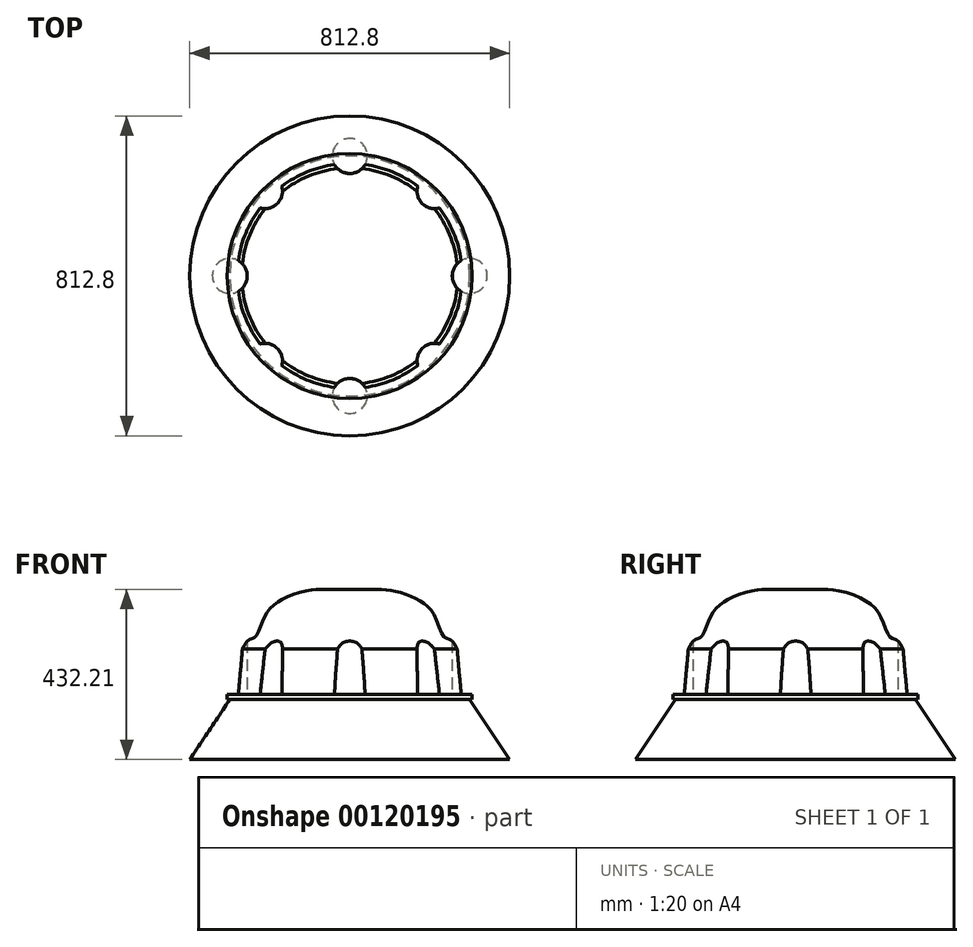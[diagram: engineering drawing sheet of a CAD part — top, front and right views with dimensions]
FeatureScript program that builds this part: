
annotation { "Feature Type Name" : "Feature", "Feature Type Description" : "" }
export const myFeature = defineFeature(function(context is Context, id is Id, definition is map)
    precondition{}
    {
        {
            var Q0;
            Q0=qCreatedBy(makeId("Front.planeOp"),FACE);
            var sketch = newSketch(context, id + "F0", { "sketchPlane" : qUnion([Q0])});
            skLineSegment(sketch, "E0", {"start": v(0, 0) * mm, "end": v(406.4, 0) * mm});
            skLineSegment(sketch, "E1", {"start": v(0, 0) * mm, "end": v(0, 152.4) * mm});
            skLineSegment(sketch, "E2", {"start": v(0, 152.4) * mm, "end": v(304.8, 152.4) * mm});
            skLineSegment(sketch, "E3", {"start": v(406.4, 0) * mm, "end": v(304.8, 152.4) * mm});
            skLineSegment(sketch, "E4", {"start": v(304.8, 152.4) * mm, "end": v(311.15, 152.4) * mm});
            skLineSegment(sketch, "E5", {"start": v(311.15, 152.4) * mm, "end": v(311.15, 165.1) * mm});
            skLineSegment(sketch, "E6", {"start": v(311.15, 165.1) * mm, "end": v(285.75, 165.1) * mm});
            skLineSegment(sketch, "E7", {"start": v(0, 152.4) * mm, "end": v(0, 304.8) * mm});
            skLineSegment(sketch, "E8", {"start": v(0, 304.8) * mm, "end": v(254, 304.8) * mm});
            skLineSegment(sketch, "E9", {"start": v(285.75, 165.1) * mm, "end": v(274.56, 280.7) * mm});
            skFitSpline(sketch, "E10", {"points": [v(274.56, 280.7) * mm, v(265.43, 295.32) * mm, v(254, 304.8) * mm, v(239.86, 311.76) * mm, v(214.22, 366.9) * mm, v(187.69, 396.64) * mm, v(151.06, 416.34) * mm, v(108.02, 429.2) * mm, v(69.08, 432.02) * mm, v(0, 432.16) * mm], "startDerivative": vector(-109.58, 198.16) * mm, "endDerivative": vector(-482.25, -1.12) * mm});
            skLineSegment(sketch, "E11", {"start": v(0, 304.8) * mm, "end": v(0, 432.16) * mm});
            skSolve(sketch);
        }
        {
            var Q0;
            Q0 = qSketchRegion(id + "F0", true);
            var Q1;
            Q1=sQuery(id+"F0.wireOp",EDGE,"E7");
            revolve(context, id + "F1", {"entities" : qUnion([Q0]), "axis" : qUnion([Q1]), "revolveType" : RevolveType.FULL});
        }
        {
            var Q0;
            Q0=makeQuery(id+"F1.opRevolve","SWEPT_FACE",FACE,{"disambiguationData":[OSD([sQuery(id+"F0.wireOp",EDGE,"E6")])]});
            var sketch = newSketch(context, id + "F2", { "sketchPlane" : qUnion([Q0])});
            skCircle(sketch, "E12", {"center": v(0, 304.8) * mm, "radius": 44.45 * mm});
            skCircle(sketch, "E13.1.0", {"center": v(-215.53, 215.53) * mm, "radius": 44.45 * mm});
            skCircle(sketch, "E13.2.0", {"center": v(-304.8, 0) * mm, "radius": 44.45 * mm});
            skCircle(sketch, "E13.3.0", {"center": v(-215.53, -215.53) * mm, "radius": 44.45 * mm});
            skCircle(sketch, "E13.4.0", {"center": v(0, -304.8) * mm, "radius": 44.45 * mm});
            skCircle(sketch, "E13.5.0", {"center": v(215.53, -215.53) * mm, "radius": 44.45 * mm});
            skCircle(sketch, "E13.6.0", {"center": v(304.8, 0) * mm, "radius": 44.45 * mm});
            skCircle(sketch, "E13.7.0", {"center": v(215.53, 215.53) * mm, "radius": 44.45 * mm});
            skPoint(sketch, "E13.center", {"position": v(0, 0) * mm});
            skSolve(sketch);
        }
        {
            var Q0;
            Q0 = qSketchRegion(id + "F2", true);
            extrude(context, id + "F3", {"entities" : qUnion([Q0]), "operationType" : NewBodyOperationType.REMOVE, "depth" : 152.4 * mm});
        }
    });
